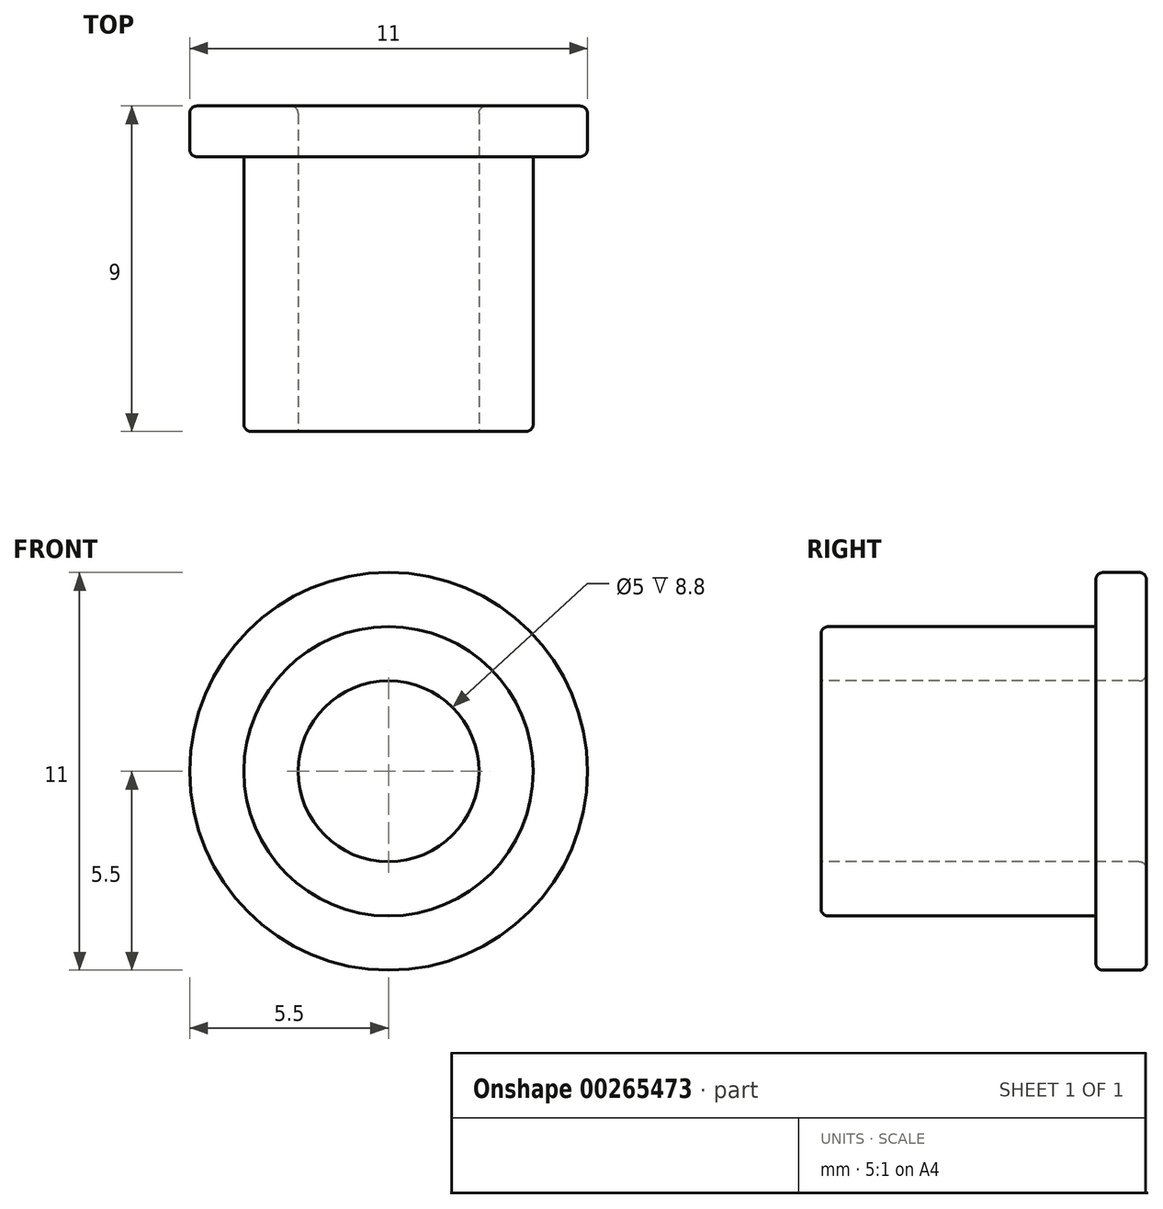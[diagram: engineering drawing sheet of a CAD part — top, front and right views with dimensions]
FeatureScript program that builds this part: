
annotation { "Feature Type Name" : "Feature", "Feature Type Description" : "" }
export const myFeature = defineFeature(function(context is Context, id is Id, definition is map)
    precondition{}
    {
        {
            var Q0;
            Q0=qCreatedBy(makeId("Front.planeOp"),FACE);
            var sketch = newSketch(context, id + "F0", { "sketchPlane" : qUnion([Q0])});
            skCircle(sketch, "E0", {"center": v(0, 0) * mm, "radius": 5.5 * mm});
            skSolve(sketch);
        }
        {
            var Q0;
            Q0=makeQuery(id+"F0.imprint","IMPRINT",FACE,{"disambiguationData":[TD([[makeQuery(id+"F0.imprint","IMPRINT",EDGE,{"derivedFrom":sQuery(id+"F0.wireOp",EDGE,"E0")}),1.0]])]});
            extrude(context, id + "F1", {"entities" : qUnion([Q0]), "depth" : 1.4 * mm});
        }
        {
            var Q0;
            Q0=makeQuery(id+"F1.opExtrude","CAP_FACE",FACE,{"disambiguationData":[OSD([sQuery(id+"F0.wireOp",EDGE,"E0")])],"isStart":false});
            var sketch = newSketch(context, id + "F2", { "sketchPlane" : qUnion([Q0])});
            skCircle(sketch, "E1", {"center": v(0, 0) * mm, "radius": 4 * mm});
            skSolve(sketch);
        }
        {
            var Q0;
            Q0=makeQuery(id+"F2.imprint","IMPRINT",FACE,{"disambiguationData":[TD([[makeQuery(id+"F2.imprint","IMPRINT",EDGE,{"derivedFrom":sQuery(id+"F2.wireOp",EDGE,"E1")}),1.0]])]});
            extrude(context, id + "F3", {"entities" : qUnion([Q0]), "operationType" : NewBodyOperationType.ADD, "depth" : 7.6 * mm});
        }
        {
            var Q0;
            Q0=makeQuery(id+"F3.opExtrude","CAP_FACE",FACE,{"disambiguationData":[OSD([sQuery(id+"F2.wireOp",EDGE,"E1")])],"isStart":false});
            var sketch = newSketch(context, id + "F4", { "sketchPlane" : qUnion([Q0])});
            skCircle(sketch, "E2", {"center": v(0, 0) * mm, "radius": 2.5 * mm});
            skSolve(sketch);
        }
        {
            var Q0;
            Q0=makeQuery(id+"F4.imprint","IMPRINT",FACE,{"disambiguationData":[TD([[makeQuery(id+"F4.imprint","IMPRINT",EDGE,{"derivedFrom":sQuery(id+"F4.wireOp",EDGE,"E2")}),1.0]])]});
            extrude(context, id + "F5", {"entities" : qUnion([Q0]), "operationType" : NewBodyOperationType.REMOVE, "oppositeDirection" : true, "depth" : 10 * mm});
        }
        {
            var Q0;
            Q0=makeQuery(id+"F5.boolean.opBoolean","COPY",EDGE,{"derivedFrom":makeQuery(id+"F5.opExtrude","CAP_EDGE",EDGE,{"disambiguationData":[OSD([sQuery(id+"F4.wireOp",EDGE,"E2")])],"isStart":true})});
            var Q1;
            Q1=makeQuery(id+"F3.opExtrude","CAP_EDGE",EDGE,{"disambiguationData":[OSD([sQuery(id+"F2.wireOp",EDGE,"E1")])],"isStart":false});
            var Q2;
            Q2=makeQuery(id+"F1.opExtrude","CAP_EDGE",EDGE,{"disambiguationData":[OSD([sQuery(id+"F0.wireOp",EDGE,"E0")])],"isStart":false});
            var Q3;
            Q3=makeQuery(id+"F1.opExtrude","CAP_EDGE",EDGE,{"disambiguationData":[OSD([sQuery(id+"F0.wireOp",EDGE,"E0")])],"isStart":true});
            var Q4;
            Q4=makeQuery(id+"F5.boolean.opBoolean","INTERSECT",EDGE,{"derivedFrom":[makeQuery(id+"F1.opExtrude","CAP_FACE",FACE,{"disambiguationData":[OSD([sQuery(id+"F0.wireOp",EDGE,"E0")])],"isStart":true}),makeQuery(id+"F5.opExtrude","SWEPT_FACE",FACE,{"disambiguationData":[OSD([sQuery(id+"F4.wireOp",EDGE,"E2")])]})]});
            fillet(context, id + "F6", {"entities" : qUnion([Q0, Q1, Q2, Q3, Q4]), "radius" : 0.2 * mm, "tangentPropagation" : true, "allowEdgeOverflow" : false});
        }
    });
